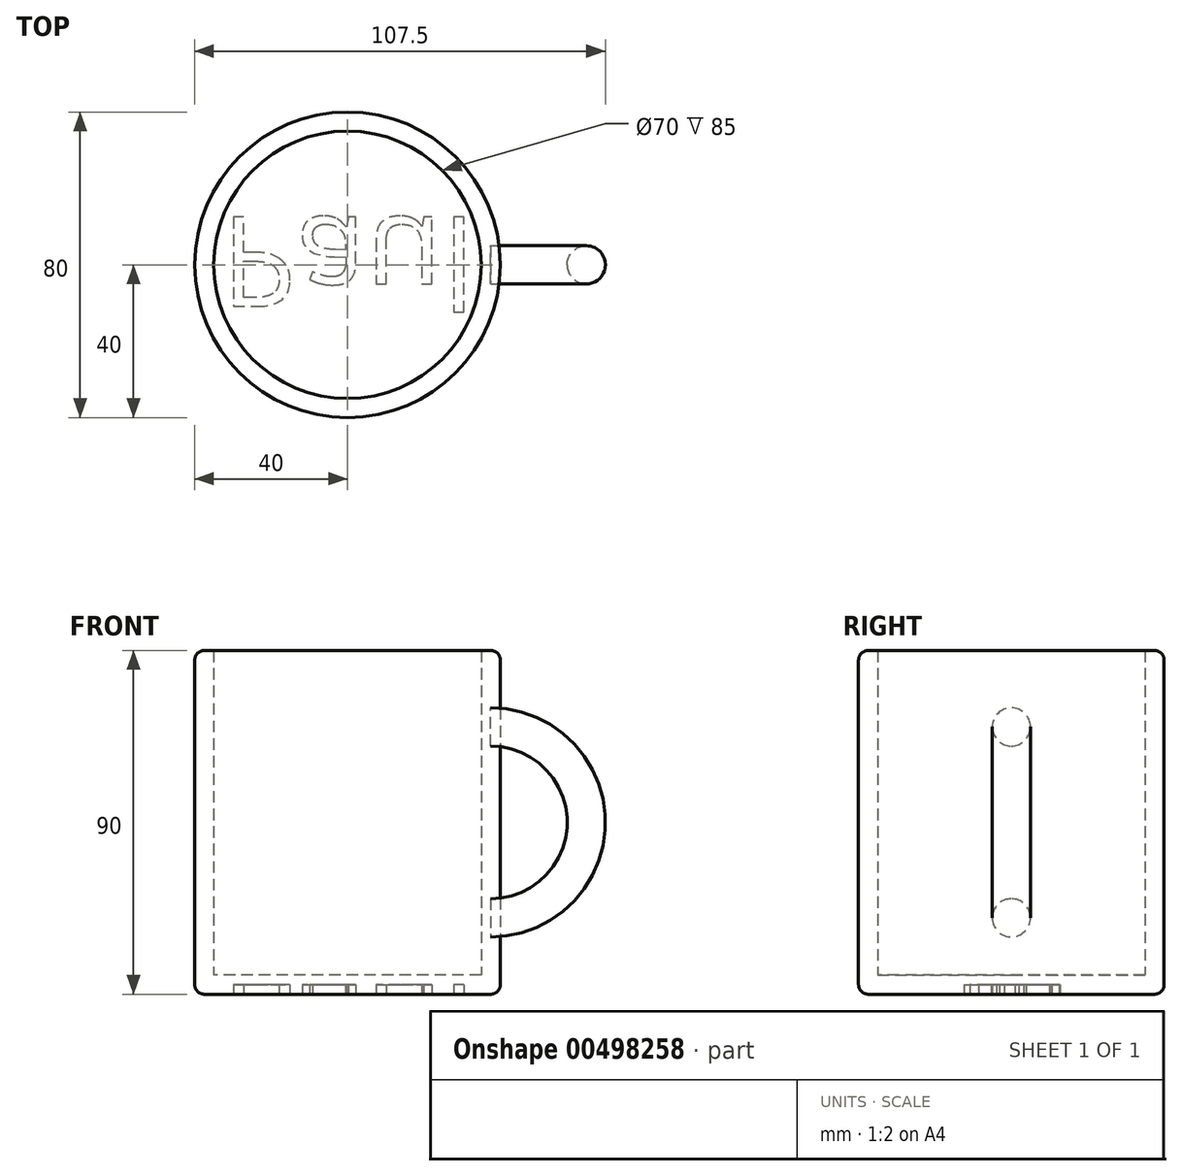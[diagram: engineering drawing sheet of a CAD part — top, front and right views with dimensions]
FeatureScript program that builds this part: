
annotation { "Feature Type Name" : "Feature", "Feature Type Description" : "" }
export const myFeature = defineFeature(function(context is Context, id is Id, definition is map)
    precondition{}
    {
        {
            var Q0;
            Q0=qCreatedBy(makeId("Top.planeOp"),FACE);
            var sketch = newSketch(context, id + "F0", { "sketchPlane" : qUnion([Q0])});
            skCircle(sketch, "E0", {"center": v(0, 0) * mm, "radius": 40 * mm});
            skSolve(sketch);
        }
        {
            var Q0;
            Q0=makeQuery(id+"F0.imprint","IMPRINT",FACE,{"disambiguationData":[TD([[makeQuery(id+"F0.imprint","IMPRINT",EDGE,{"derivedFrom":sQuery(id+"F0.wireOp",EDGE,"E0")}),1.0]])]});
            extrude(context, id + "F1", {"entities" : qUnion([Q0]), "depth" : 90 * mm});
        }
        {
            var Q0;
            Q0=makeQuery(id+"F1.opExtrude","CAP_FACE",FACE,{"disambiguationData":[OSD([sQuery(id+"F0.wireOp",EDGE,"E0")])],"isStart":false});
            shell(context, id + "F2", {"entities" : qUnion([Q0]), "thickness" : 5 * mm});
        }
        {
            var Q0;
            Q0=qCreatedBy(makeId("Right.planeOp"),FACE);
            cPlane(context, id + "F3", {"entities" : qUnion([Q0]), "cplaneType" : CPlaneType.OFFSET, "offset" : 37.5 * mm, "width" : 150 * mm, "height" : 150 * mm});
        }
        {
            var Q0;
            Q0=qCreatedBy(id+"F3.planeOp",FACE);
            var sketch = newSketch(context, id + "F4", { "sketchPlane" : qUnion([Q0])});
            skCircle(sketch, "E1", {"center": v(0, 70) * mm, "radius": 5 * mm});
            skLineSegment(sketch, "E2", {"start": v(0, 45) * mm, "end": v(27.52, 45) * mm});
            skSolve(sketch);
        }
        {
            var Q0;
            Q0 = qSketchRegion(id + "F4", true);
            var Q1;
            Q1=sQuery(id+"F4.wireOp",EDGE,"E2");
            revolve(context, id + "F5", {"entities" : qUnion([Q0]), "axis" : qUnion([Q1]), "revolveType" : RevolveType.ONE_DIRECTION, "angle" : 180 * degree});
        }
        {
            var Q0;
            Q0=makeQuery(id+"F1.opExtrude","CAP_EDGE",EDGE,{"disambiguationData":[OSD([sQuery(id+"F0.wireOp",EDGE,"E0")])],"isStart":false});
            var Q1;
            Q1=makeQuery(id+"F1.opExtrude","CAP_EDGE",EDGE,{"disambiguationData":[OSD([sQuery(id+"F0.wireOp",EDGE,"E0")])],"isStart":true});
            fillet(context, id + "F6", {"entities" : qUnion([Q0, Q1]), "radius" : 2.5 * mm, "tangentPropagation" : true, "allowEdgeOverflow" : false});
        }
        {
            var Q0;
            Q0=makeQuery(id+"F1.opExtrude","CAP_FACE",FACE,{"disambiguationData":[OSD([sQuery(id+"F0.wireOp",EDGE,"E0")])],"isStart":true});
            var sketch = newSketch(context, id + "F7", { "sketchPlane" : qUnion([Q0])});
            skText(sketch, "E3", { "text": "Paul\n", "fontName": "OpenSans-Regular.ttf"});
            const initialGuessF7  = {"E3": [-0.03312, -0.0125, 1, 0, 0.02359]};
            skSetInitialGuess(sketch, initialGuessF7);
            skSolve(sketch);
        }
        {
            var Q0;
            Q0 = qSketchRegion(id + "F7", true);
            extrude(context, id + "F8", {"entities" : qUnion([Q0]), "operationType" : NewBodyOperationType.REMOVE, "oppositeDirection" : true, "depth" : 2.5 * mm});
        }
    });
